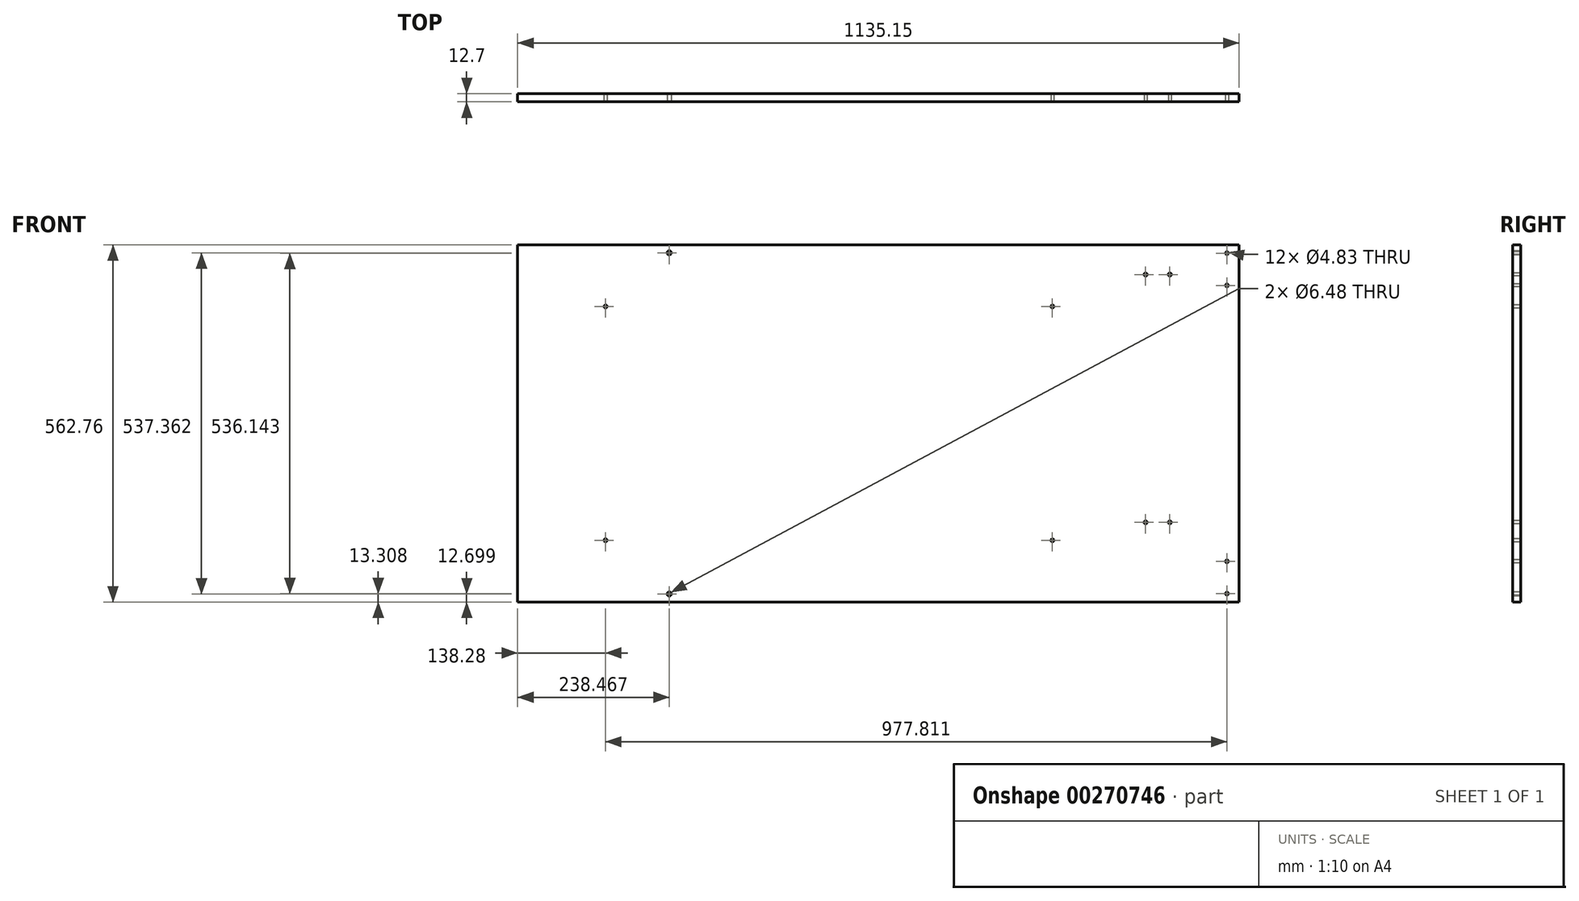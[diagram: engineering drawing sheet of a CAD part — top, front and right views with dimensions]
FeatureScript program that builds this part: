
annotation { "Feature Type Name" : "Feature", "Feature Type Description" : "" }
export const myFeature = defineFeature(function(context is Context, id is Id, definition is map)
    precondition{}
    {
        {
            var Q0;
            Q0=qCreatedBy(makeId("Front.planeOp"),FACE);
            var sketch = newSketch(context, id + "F0", { "sketchPlane" : qUnion([Q0])});
            skLineSegment(sketch, "E0.bottom", {"start": v(293.73, 281.38) * mm, "end": v(-381, 281.38) * mm});
            skLineSegment(sketch, "E0.top", {"start": v(293.73, -281.38) * mm, "end": v(-381, -281.38) * mm});
            skPoint(sketch, "E0.middle", {"position": v(0, 0) * mm});
            skPoint(sketch, "E1.left.start.orphan", {"position": v(330.2, 127) * mm});
            skPoint(sketch, "E2.orphan", {"position": v(330.2, -127) * mm});
            skPoint(sketch, "E3.middle", {"position": v(-381, 0) * mm});
            skPoint(sketch, "E4.orphan", {"position": v(-381, -127) * mm});
            skLineSegment(sketch, "E5", {"start": v(-400.15, -139.7) * mm, "end": v(-381, -139.7) * mm});
            skLineSegment(sketch, "E6", {"start": v(-381, 281.38) * mm, "end": v(-736.6, 281.38) * mm});
            skPoint(sketch, "E6.endSnap0", {"position": v(-736.6, 139.7) * mm});
            skLineSegment(sketch, "E7", {"start": v(-736.6, -281.38) * mm, "end": v(-381, -281.38) * mm});
            skLineSegment(sketch, "E8", {"start": v(293.73, 281.38) * mm, "end": v(293.73, -281.38) * mm});
            skPoint(sketch, "E0.left.end.orphan", {"position": v(381, -281.38) * mm});
            skPoint(sketch, "E9.orphan", {"position": v(381, 281.38) * mm});
            skLineSegment(sketch, "E10", {"start": v(-736.6, 281.38) * mm, "end": v(-780.24, 281.38) * mm});
            skLineSegment(sketch, "E11", {"start": v(-780.24, -281.38) * mm, "end": v(-736.6, -281.38) * mm});
            skPoint(sketch, "E12.orphan", {"position": v(-823.88, 281.38) * mm});
            skLineSegment(sketch, "E13", {"start": v(-780.24, 281.38) * mm, "end": v(-802.06, 281.38) * mm});
            skLineSegment(sketch, "E14", {"start": v(-802.06, -281.38) * mm, "end": v(-780.24, -281.38) * mm});
            skLineSegment(sketch, "E15", {"start": v(-802.06, 281.38) * mm, "end": v(-803.33, 281.38) * mm});
            skLineSegment(sketch, "E16", {"start": v(-803.33, -281.38) * mm, "end": v(-802.06, -281.38) * mm});
            skLineSegment(sketch, "E17", {"start": v(-803.33, -281.38) * mm, "end": v(-841.42, -281.38) * mm});
            skLineSegment(sketch, "E18", {"start": v(-841.42, -281.38) * mm, "end": v(-841.42, 281.38) * mm});
            skLineSegment(sketch, "E19", {"start": v(-841.42, 281.38) * mm, "end": v(-802.06, 281.38) * mm});
            skSolve(sketch);
        }
        {
            var Q0;
            Q0=qSketchRegion(id+"F0",true);
            extrude(context, id + "F1", {"entities" : qUnion([Q0]), "depth" : 12.7 * mm});
        }
        {
            var Q0;
            Q0=makeQuery(id+"F1.opExtrude","CAP_FACE",FACE,{"disambiguationData":[OSD([sQuery(id+"F0.wireOp",EDGE,"E0.bottom"),sQuery(id+"F0.wireOp",EDGE,"E0.top"),sQuery(id+"F0.wireOp",EDGE,"E0.left"),sQuery(id+"F0.wireOp",EDGE,"E0.right"),sQuery(id+"F0.wireOp",EDGE,"6b8f2743-ba3a-41ed-b816-415a804c3c5f.trimOffspring"),sQuery(id+"F0.wireOp",EDGE,"rUNp1Zjr-m9Tr-Jaki-lSlT-tGsEQWeUejhB"),sQuery(id+"F0.wireOp",EDGE,"512u1cFn-DseQ-SAyc-m0Mc-sPxMefES2NVM"),sQuery(id+"F0.wireOp",EDGE,"EMFdw8Zb-boA4-zE6l-Ll2B-hDPI1YFg69C0"),sQuery(id+"F0.wireOp",EDGE,"lgyBSfzd-YJOu-PVTn-TOih-Goa29ghgCUQV"),sQuery(id+"F0.wireOp",EDGE,"E5")])],"isStart":false});
            var sketch = newSketch(context, id + "F2", { "sketchPlane" : qUnion([Q0])});
            skPoint(sketch, "E20", {"position": v(184.79, 234.48) * mm});
            skPoint(sketch, "E21", {"position": v(146.62, 234.48) * mm});
            skPoint(sketch, "E22", {"position": v(146.62, -155.85) * mm});
            skPoint(sketch, "E23", {"position": v(184.79, -155.85) * mm});
            skPoint(sketch, "E24", {"position": v(237.71, 268.07) * mm});
            skPoint(sketch, "E25", {"position": v(247.87, 268.07) * mm});
            skPoint(sketch, "E26", {"position": v(250.41, 268.07) * mm});
            skLineSegment(sketch, "E27", {"start": v(247.87, 268.07) * mm, "end": v(249.14, 268.07) * mm});
            skPoint(sketch, "E28", {"position": v(249.14, 268.07) * mm});
            skLineSegment(sketch, "E29", {"start": v(249.14, 268.07) * mm, "end": v(249.4, 268.07) * mm});
            skPoint(sketch, "E30", {"position": v(249.4, 268.07) * mm});
            skLineSegment(sketch, "E31", {"start": v(249.4, 268.07) * mm, "end": v(249.27, 268.07) * mm});
            skPoint(sketch, "E32", {"position": v(249.27, 268.07) * mm});
            skLineSegment(sketch, "E33", {"start": v(381, 0) * mm, "end": v(223.6, 0) * mm});
            skPoint(sketch, "E33.endSnap0", {"position": v(381, 0) * mm});
            skPoint(sketch, "E34.MirrorP", {"position": v(249.27, -268.07) * mm});
            skLineSegment(sketch, "E35", {"start": v(249.27, -268.07) * mm, "end": v(274.67, -268.07) * mm});
            skPoint(sketch, "E36", {"position": v(274.67, -268.07) * mm});
            skPoint(sketch, "E37", {"position": v(274.67, 268.07) * mm});
            skPoint(sketch, "E38", {"position": v(274.67, -217.27) * mm});
            skPoint(sketch, "E39.MirrorP", {"position": v(274.67, 217.27) * mm});
            skLineSegment(sketch, "E40", {"start": v(274.67, 217.27) * mm, "end": v(293.72, 217.27) * mm});
            skSolve(sketch);
        }
        {
            var Q0;
            Q0=sQuery(id+"F2.wireOp",VERTEX,"E20");
            var Q1;
            Q1=sQuery(id+"F2.wireOp",VERTEX,"E21");
            var Q2;
            Q2=sQuery(id+"F2.wireOp",VERTEX,"E23");
            var Q3;
            Q3=sQuery(id+"F2.wireOp",VERTEX,"E22");
            var Q4;
            Q4=sQuery(id+"F2.wireOp",VERTEX,"E35.end");
            var Q5;
            Q5=sQuery(id+"F2.wireOp",VERTEX,"E37");
            var Q6;
            Q6=sQuery(id+"F2.wireOp",VERTEX,"E39.MirrorP");
            var Q7;
            Q7=sQuery(id+"F2.wireOp",VERTEX,"E38");
            var Q8;
            Q8=makeQuery(id+"F1.opExtrude","SWEPT_BODY",BODY,{"disambiguationData":[OSD([sQuery(id+"F0.wireOp",EDGE,"E0.bottom"),sQuery(id+"F0.wireOp",EDGE,"E0.top"),sQuery(id+"F0.wireOp",EDGE,"E0.left"),sQuery(id+"F0.wireOp",EDGE,"E6"),sQuery(id+"F0.wireOp",EDGE,"Rqzt7koN-vXU3-RKIl-bBzC-r2Zxxo2AtwCc"),sQuery(id+"F0.wireOp",EDGE,"E7")])]});
            hole(context, id + "F3", {"style" : HoleStyle.SIMPLE, "endStyle" : HoleEndStyle.THROUGH, "holeDiameter" : 4.83 * mm, "tappedDepth" : 12.7 * mm, "tapClearance" : 3, "locations" : qUnion([Q0, Q1, Q2, Q3, Q4, Q5, Q6, Q7]), "scope" : qUnion([Q8])});
        }
        {
            var Q0;
            Q0=makeQuery(id+"F1.opExtrude","CAP_FACE",FACE,{"disambiguationData":[OSD([sQuery(id+"F0.wireOp",EDGE,"E0.bottom"),sQuery(id+"F0.wireOp",EDGE,"E0.top"),sQuery(id+"F0.wireOp",EDGE,"E6"),sQuery(id+"F0.wireOp",EDGE,"E7"),sQuery(id+"F0.wireOp",EDGE,"E8"),sQuery(id+"F0.wireOp",EDGE,"E11"),sQuery(id+"F0.wireOp",EDGE,"E10"),sQuery(id+"F0.wireOp",EDGE,"E13"),sQuery(id+"F0.wireOp",EDGE,"E14"),sQuery(id+"F0.wireOp",EDGE,"E15"),sQuery(id+"F0.wireOp",EDGE,"E16"),sQuery(id+"F0.wireOp",EDGE,"bNuqvtO5-wbpF-1hN6-XCZh-rtWMtZmRpUNC")])],"isStart":false});
            var sketch = newSketch(context, id + "F4", { "sketchPlane" : qUnion([Q0])});
            skLineSegment(sketch, "E41", {"start": v(-803.33, -281.38) * mm, "end": v(-803.33, -268.68) * mm});
            skLineSegment(sketch, "E42", {"start": v(-803.33, -268.68) * mm, "end": v(-602.95, -268.68) * mm});
            skPoint(sketch, "E43", {"position": v(-602.95, -268.68) * mm});
            skLineSegment(sketch, "E44", {"start": v(-803.33, 0) * mm, "end": v(-684.9, 0) * mm});
            skPoint(sketch, "E44.endSnap0", {"position": v(-803.33, 0) * mm});
            skPoint(sketch, "E45.MirrorP", {"position": v(-602.95, 268.68) * mm});
            skSolve(sketch);
        }
        {
            var Q0;
            Q0=sQuery(id+"F4.wireOp",VERTEX,"E43");
            var Q1;
            Q1=sQuery(id+"F4.wireOp",VERTEX,"E45.MirrorP");
            var Q2;
            Q2=makeQuery(id+"F1.opExtrude","SWEPT_BODY",BODY,{"disambiguationData":[OSD([sQuery(id+"F0.wireOp",EDGE,"E0.bottom"),sQuery(id+"F0.wireOp",EDGE,"E0.top"),sQuery(id+"F0.wireOp",EDGE,"E6"),sQuery(id+"F0.wireOp",EDGE,"E7"),sQuery(id+"F0.wireOp",EDGE,"E8"),sQuery(id+"F0.wireOp",EDGE,"E11"),sQuery(id+"F0.wireOp",EDGE,"E10"),sQuery(id+"F0.wireOp",EDGE,"E13"),sQuery(id+"F0.wireOp",EDGE,"E14"),sQuery(id+"F0.wireOp",EDGE,"E15"),sQuery(id+"F0.wireOp",EDGE,"E16"),sQuery(id+"F0.wireOp",EDGE,"bNuqvtO5-wbpF-1hN6-XCZh-rtWMtZmRpUNC")])]});
            hole(context, id + "F5", {"style" : HoleStyle.SIMPLE, "endStyle" : HoleEndStyle.THROUGH, "holeDiameter" : 6.48 * mm, "tappedDepth" : 12.7 * mm, "tapClearance" : 3, "locations" : qUnion([Q0, Q1]), "scope" : qUnion([Q2])});
        }
        {
            var Q0;
            Q0=makeQuery(id+"F1.opExtrude","CAP_FACE",FACE,{"disambiguationData":[OSD([sQuery(id+"F0.wireOp",EDGE,"E0.bottom"),sQuery(id+"F0.wireOp",EDGE,"E0.top"),sQuery(id+"F0.wireOp",EDGE,"E6"),sQuery(id+"F0.wireOp",EDGE,"E7"),sQuery(id+"F0.wireOp",EDGE,"E8"),sQuery(id+"F0.wireOp",EDGE,"E11"),sQuery(id+"F0.wireOp",EDGE,"E10"),sQuery(id+"F0.wireOp",EDGE,"E13"),sQuery(id+"F0.wireOp",EDGE,"E14"),sQuery(id+"F0.wireOp",EDGE,"E15"),sQuery(id+"F0.wireOp",EDGE,"E16"),sQuery(id+"F0.wireOp",EDGE,"bNuqvtO5-wbpF-1hN6-XCZh-rtWMtZmRpUNC")])],"isStart":false});
            var sketch = newSketch(context, id + "F6", { "sketchPlane" : qUnion([Q0])});
            skLineSegment(sketch, "E46", {"start": v(-803.33, 0) * mm, "end": v(-803.33, 184.14) * mm});
            skLineSegment(sketch, "E47", {"start": v(-803.33, 184.14) * mm, "end": v(-803.33, -184.14) * mm});
            skLineSegment(sketch, "E48", {"start": v(-602.95, -268.68) * mm, "end": v(-602.95, -184.14) * mm});
            skLineSegment(sketch, "E49", {"start": v(-602.95, -184.14) * mm, "end": v(-803.33, -184.14) * mm});
            skPoint(sketch, "E50", {"position": v(-703.14, -184.14) * mm});
            skLineSegment(sketch, "E51", {"start": v(-803.33, 0) * mm, "end": v(-725.97, 0) * mm});
            skPoint(sketch, "E52.MirrorP", {"position": v(-703.14, 184.14) * mm});
            skLineSegment(sketch, "E53", {"start": v(-703.14, -184.14) * mm, "end": v(0, -184.14) * mm});
            skPoint(sketch, "E54", {"position": v(0, -184.14) * mm});
            skPoint(sketch, "E55.MirrorP", {"position": v(0, 184.14) * mm});
            skSolve(sketch);
        }
        {
            var Q0;
            Q0=sQuery(id+"F6.wireOp",VERTEX,"E52.MirrorP");
            var Q1;
            Q1=sQuery(id+"F6.wireOp",VERTEX,"E50");
            var Q2;
            Q2=sQuery(id+"F6.wireOp",VERTEX,"E55.MirrorP");
            var Q3;
            Q3=sQuery(id+"F6.wireOp",VERTEX,"E54");
            var Q4;
            Q4=makeQuery(id+"F1.opExtrude","SWEPT_BODY",BODY,{"disambiguationData":[OSD([sQuery(id+"F0.wireOp",EDGE,"E0.bottom"),sQuery(id+"F0.wireOp",EDGE,"E0.top"),sQuery(id+"F0.wireOp",EDGE,"E6"),sQuery(id+"F0.wireOp",EDGE,"E7"),sQuery(id+"F0.wireOp",EDGE,"E8"),sQuery(id+"F0.wireOp",EDGE,"E11"),sQuery(id+"F0.wireOp",EDGE,"E10"),sQuery(id+"F0.wireOp",EDGE,"E13"),sQuery(id+"F0.wireOp",EDGE,"E14"),sQuery(id+"F0.wireOp",EDGE,"E15"),sQuery(id+"F0.wireOp",EDGE,"E16"),sQuery(id+"F0.wireOp",EDGE,"bNuqvtO5-wbpF-1hN6-XCZh-rtWMtZmRpUNC")])]});
            hole(context, id + "F7", {"style" : HoleStyle.SIMPLE, "endStyle" : HoleEndStyle.THROUGH, "holeDiameter" : 4.83 * mm, "tappedDepth" : 12.7 * mm, "tapClearance" : 3, "locations" : qUnion([Q0, Q1, Q2, Q3]), "scope" : qUnion([Q4])});
        }
    });
